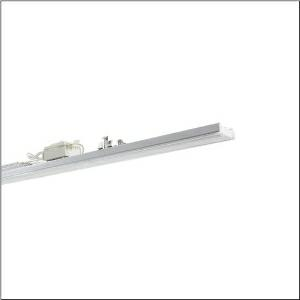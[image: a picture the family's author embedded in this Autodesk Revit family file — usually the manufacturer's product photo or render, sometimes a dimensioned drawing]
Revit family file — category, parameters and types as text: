
# Revit family: licross_11_recessed_mo_51te187n485g
name_source: partatom
category: Lighting Fixtures
units: mm (PartAtom-declared; Revit-internal decimal feet)

## family parameters
Cut with Voids When Loaded = No
Host = Face
Light Source = No
Part Type = Normal
Room Calculation Point = No
Round Connector Dimension = Use Diameter
Shared = No

## types (1)
- Licross 11 Recessed MO (1 x LED, 8700 lm, 48.5 W, 4000K)
    Apparent Load = 49 VA
    CIE Flux Codes = 83 96 99 100 100
    Color Rendering = 80
    Color Temperature = 4000K
    Default Elevation = 1800 mm
    Description = Licross 11 Recessed MO, luminaire insert, of sheet steel, galvanised, coil coated, white, length: 1.500mm, width: 66mm, height: 67mm, LED rated luminous flux: 8.700lm, light colour: 840, SDCM (Standard Deviation of Colour Matching)MacAdam ≤ 2 SDCM (initial), control gear: ON/OFF, with plug, 3-pole, with phase selection, mains connection: 220..240V, AC, 50/60Hz, rated input power: 49W, internal wiring halogen-free, primary light control with lens, of plastic, primary optical cover: cover, of PMMA, light emission: direct distribution, primary light characteristic: symmetric, protection rating (complete): IP54, insulation class (complete): insulation class I (protective earthing), certification: CE, ENEC, VDE, UKCA, protection symbol: D if used in an environment with non-conductive dust loads with corresponding accessories, impact resistance: IK06, permissible ambient temperature for indoor applications: -35..+35°C, corresponds to IFS (International Featured Standards) requirements for safety and quality in the food industry, reducing of maximum allowable ambient temperature of 5°C with ceiling mounting, The light source and the operating device comply with the requirements of the Ecodesign Regulation (EU) 2019/2020 and are replaceable in accordance with this regulation, packaging unit: 1 piece
    Height = 58 mm
    Lamp = 1 x LED
    Lamp Light Flux = 8700 lm
    Lamp Power = 48.5 W
    Lamp count = 1
    Length = 1500 mm
    Luminous efficacy = 179 lm/W
    Manufacturer = Siteco
    ModVariant = No
    Model = 51TE187N485G
    Mounting Place = Ceiling
    Mounting Type = Pendant
    Number of Poles = 1
    OnlyDefault = Yes
    Power Factor = 1
    Product Name = Licross 11 Recessed MO
    Product group = luminaire insert | ceiling pendant
    ProductGroupID = 901
    Protection Class = Protection class I
    Protection Degree = IP 54
    RLX_Detail_Level = 1
    RLX_Emergency_Light_Flux = 0 lm
    RLX_Emergency_Type = 0
    RLX_Emergency_Type_DB = No
    RlxData = <blob elided: 21057 chars, md5=d7548d6f>
    Socket = socket
    Standby Power = 0 W
    System Light Flux = 8700 lm
    System Power = 49 W
    Type Comments = Product without accessories
    Type Image = l_1296930.jpg
    URL = http://relux.com
    VarID = ---
    Voltage = 0 V
    Weight = 0.00 kg
    Width = 66 mm

## geometry (parser evidence)
native form markers: Blend x4, Sweep x9
no freeform markers — native parametric forms only
